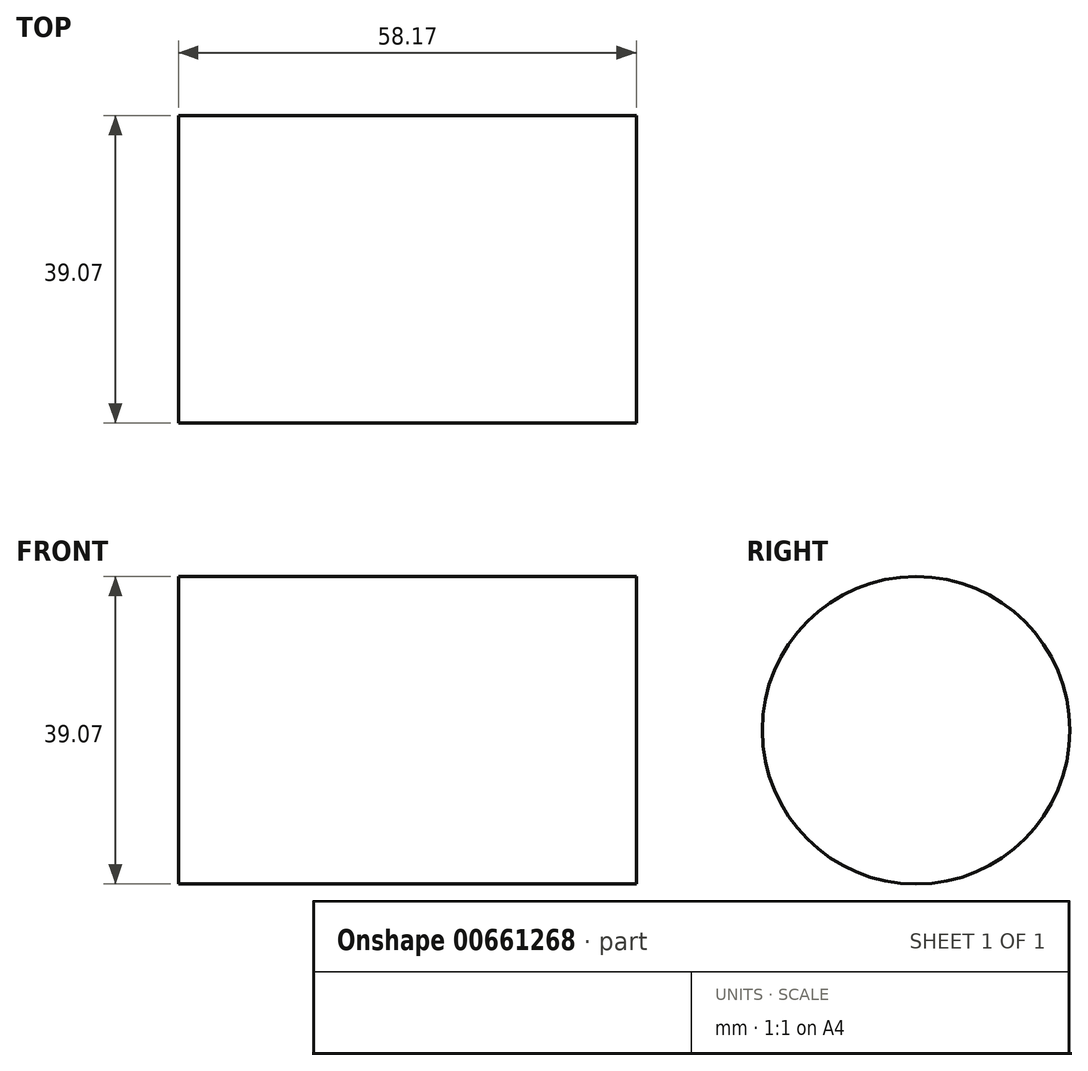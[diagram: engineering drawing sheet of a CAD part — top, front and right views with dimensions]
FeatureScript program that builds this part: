
annotation { "Feature Type Name" : "Feature", "Feature Type Description" : "" }
export const myFeature = defineFeature(function(context is Context, id is Id, definition is map)
    precondition{}
    {
        {
            var Q0;
            Q0=qCreatedBy(makeId("Right.planeOp"),FACE);
            var sketch = newSketch(context, id + "F0", { "sketchPlane" : qUnion([Q0])});
            skCircle(sketch, "E0", {"center": v(38.12, 30.7) * mm, "radius": 19.53 * mm});
            skSolve(sketch);
        }
        {
            var Q0;
            Q0 = qSketchRegion(id + "F0", true);
            extrude(context, id + "F1", {"entities" : qUnion([Q0]), "oppositeDirection" : true, "depth" : 58.17 * mm, "offsetDistance" : 25.4 * mm});
        }
    });
